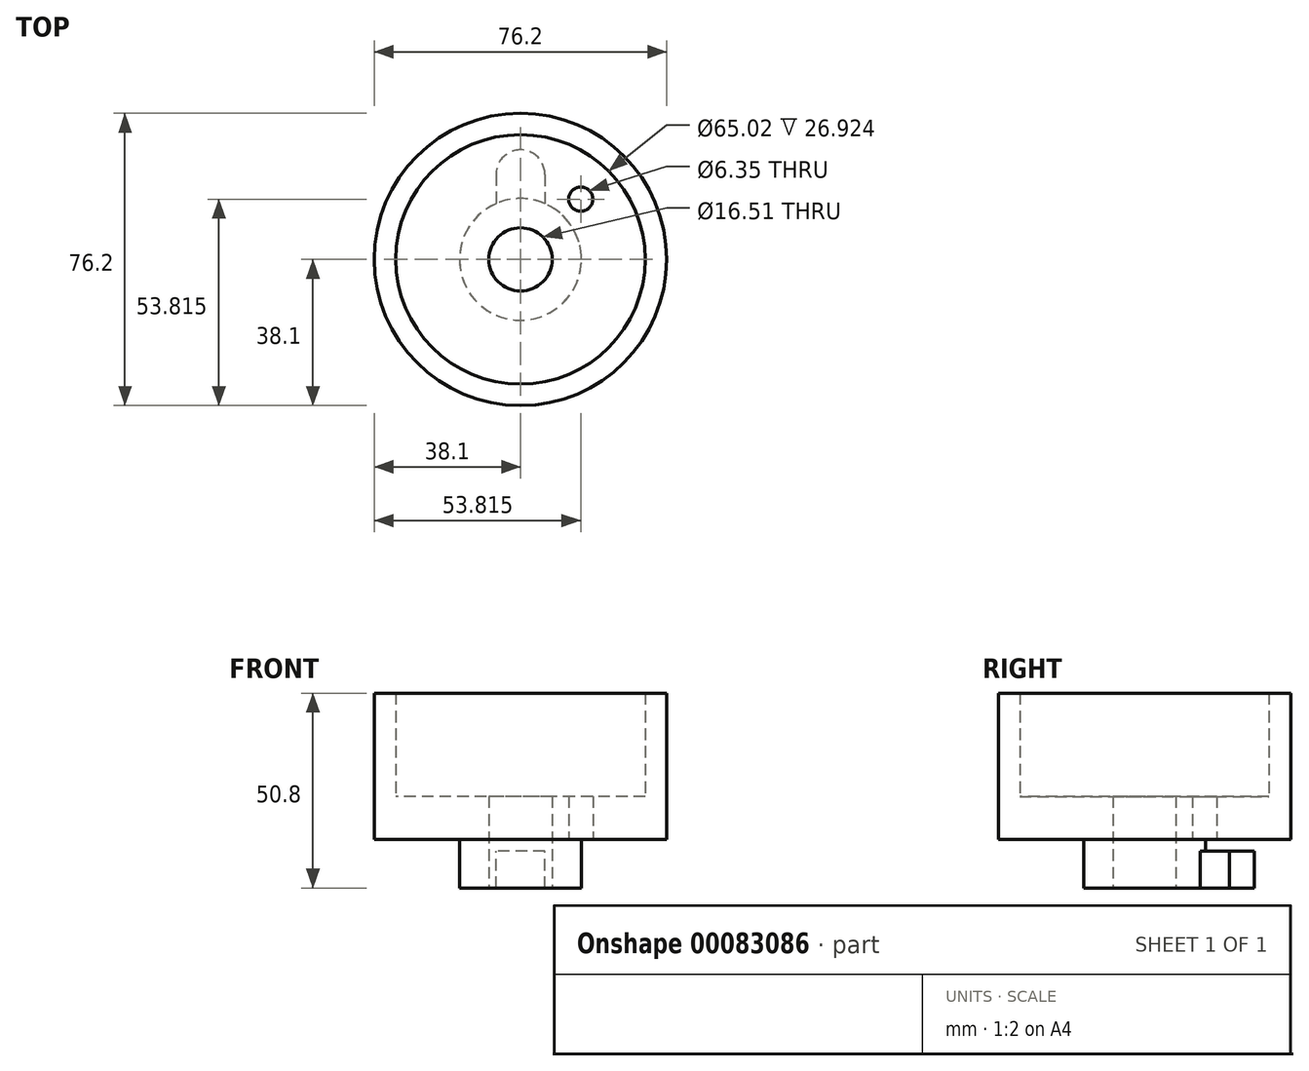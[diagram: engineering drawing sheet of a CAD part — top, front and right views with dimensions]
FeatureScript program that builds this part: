
annotation { "Feature Type Name" : "Feature", "Feature Type Description" : "" }
export const myFeature = defineFeature(function(context is Context, id is Id, definition is map)
    precondition{}
    {
        {
            var Q0;
            Q0=qCreatedBy(makeId("Top.planeOp"),FACE);
            var sketch = newSketch(context, id + "F0", { "sketchPlane" : qUnion([Q0])});
            skCircle(sketch, "E0", {"center": v(0, 0) * mm, "radius": 32.51 * mm});
            skCircle(sketch, "E1", {"center": v(0, 0) * mm, "radius": 38.1 * mm});
            skCircle(sketch, "E2", {"center": v(0, 0) * mm, "radius": 8.26 * mm});
            skCircle(sketch, "E3", {"center": v(0, 0) * mm, "radius": 15.88 * mm});
            skPoint(sketch, "E4", {"position": v(0, 22.22) * mm});
            skCircle(sketch, "E5", {"center": v(0, 22.22) * mm, "radius": 6.35 * mm});
            skPoint(sketch, "E6", {"position": v(-6.35, 22.22) * mm});
            skPoint(sketch, "E7", {"position": v(-6.35, 14.55) * mm});
            skPoint(sketch, "E8", {"position": v(6.35, 22.14) * mm});
            skPoint(sketch, "E9", {"position": v(6.35, 14.55) * mm});
            skLineSegment(sketch, "E10", {"start": v(-6.35, 22.22) * mm, "end": v(-6.35, 14.55) * mm});
            skLineSegment(sketch, "E11", {"start": v(6.35, 22.14) * mm, "end": v(6.35, 14.55) * mm});
            skPoint(sketch, "E12", {"position": v(15.72, 15.72) * mm});
            skCircle(sketch, "E13", {"center": v(15.72, 15.72) * mm, "radius": 3.18 * mm});
            skSolve(sketch);
        }
        {
            var Q0;
            Q0 = qSketchRegion(id + "F0", true);
            extrude(context, id + "F1", {"entities" : qUnion([Q0]), "depth" : 38.1 * mm});
        }
        {
            var Q0;
            Q0=makeQuery(id+"F0.imprint","IMPRINT",FACE,{"disambiguationData":[TD([[makeQuery(id+"F0.imprint","IMPRINT",EDGE,{"derivedFrom":sQuery(id+"F0.wireOp",EDGE,"E0")}),1.0]])]});
            var Q1;
            {var subQ0=sQuery(id+"F0.wireOp",EDGE,"E5");var subQ1=makeQuery(id+"F0.imprint","INTERSECT",VERTEX,{"derivedFrom":[subQ0,sQuery(id+"F0.wireOp",EDGE,"E10")]});Q1=makeQuery(id+"F0.imprint","IMPRINT",FACE,{"disambiguationData":[TD([[makeQuery(id+"F0.imprint","IMPRINT",EDGE,{"disambiguationData":[TD([[subQ1,-1.0]])],"derivedFrom":subQ0}),1.0]])]});}
            var Q2;
            {var subQ0=sQuery(id+"F0.wireOp",EDGE,"E11");Q2=makeQuery(id+"F0.imprint","IMPRINT",FACE,{"disambiguationData":[TD([[makeQuery(id+"F0.imprint","IMPRINT",EDGE,{"derivedFrom":subQ0}),-1.0]])]});}
            var Q3;
            {var subQ0=sQuery(id+"F0.wireOp",EDGE,"E10");Q3=makeQuery(id+"F0.imprint","IMPRINT",FACE,{"disambiguationData":[TD([[makeQuery(id+"F0.imprint","IMPRINT",EDGE,{"derivedFrom":subQ0}),1.0]])]});}
            extrude(context, id + "F2", {"entities" : qUnion([Q0, Q1, Q2, Q3]), "operationType" : NewBodyOperationType.ADD, "depth" : 11.18 * mm});
        }
        {
            var Q0;
            Q0=makeQuery(id+"F0.imprint","IMPRINT",FACE,{"disambiguationData":[TD([[makeQuery(id+"F0.imprint","IMPRINT",EDGE,{"derivedFrom":sQuery(id+"F0.wireOp",EDGE,"E2")}),-1.0]])]});
            extrude(context, id + "F3", {"entities" : qUnion([Q0]), "operationType" : NewBodyOperationType.ADD, "depth" : 11.18 * mm, "hasSecondDirection" : true, "secondDirectionOppositeDirection" : true, "secondDirectionDepth" : 12.7 * mm});
        }
        {
            var Q0;
            {var subQ0=sQuery(id+"F0.wireOp",EDGE,"E5");var subQ1=makeQuery(id+"F0.imprint","INTERSECT",VERTEX,{"derivedFrom":[subQ0,sQuery(id+"F0.wireOp",EDGE,"E10")]});Q0=makeQuery(id+"F0.imprint","IMPRINT",FACE,{"disambiguationData":[TD([[makeQuery(id+"F0.imprint","IMPRINT",EDGE,{"disambiguationData":[TD([[subQ1,-1.0]])],"derivedFrom":subQ0}),1.0]])]});}
            var Q1;
            {var subQ0=sQuery(id+"F0.wireOp",EDGE,"E10");Q1=makeQuery(id+"F0.imprint","IMPRINT",FACE,{"disambiguationData":[TD([[makeQuery(id+"F0.imprint","IMPRINT",EDGE,{"derivedFrom":subQ0}),1.0]])]});}
            var Q2;
            {var subQ0=sQuery(id+"F0.wireOp",EDGE,"E11");Q2=makeQuery(id+"F0.imprint","IMPRINT",FACE,{"disambiguationData":[TD([[makeQuery(id+"F0.imprint","IMPRINT",EDGE,{"derivedFrom":subQ0}),-1.0]])]});}
            extrude(context, id + "F4", {"entities" : qUnion([Q0, Q1, Q2]), "operationType" : NewBodyOperationType.ADD, "oppositeDirection" : true, "depth" : 12.7 * mm, "hasSecondDirection" : true, "secondDirectionOppositeDirection" : true, "secondDirectionDepth" : 3.05 * mm});
        }
    });
